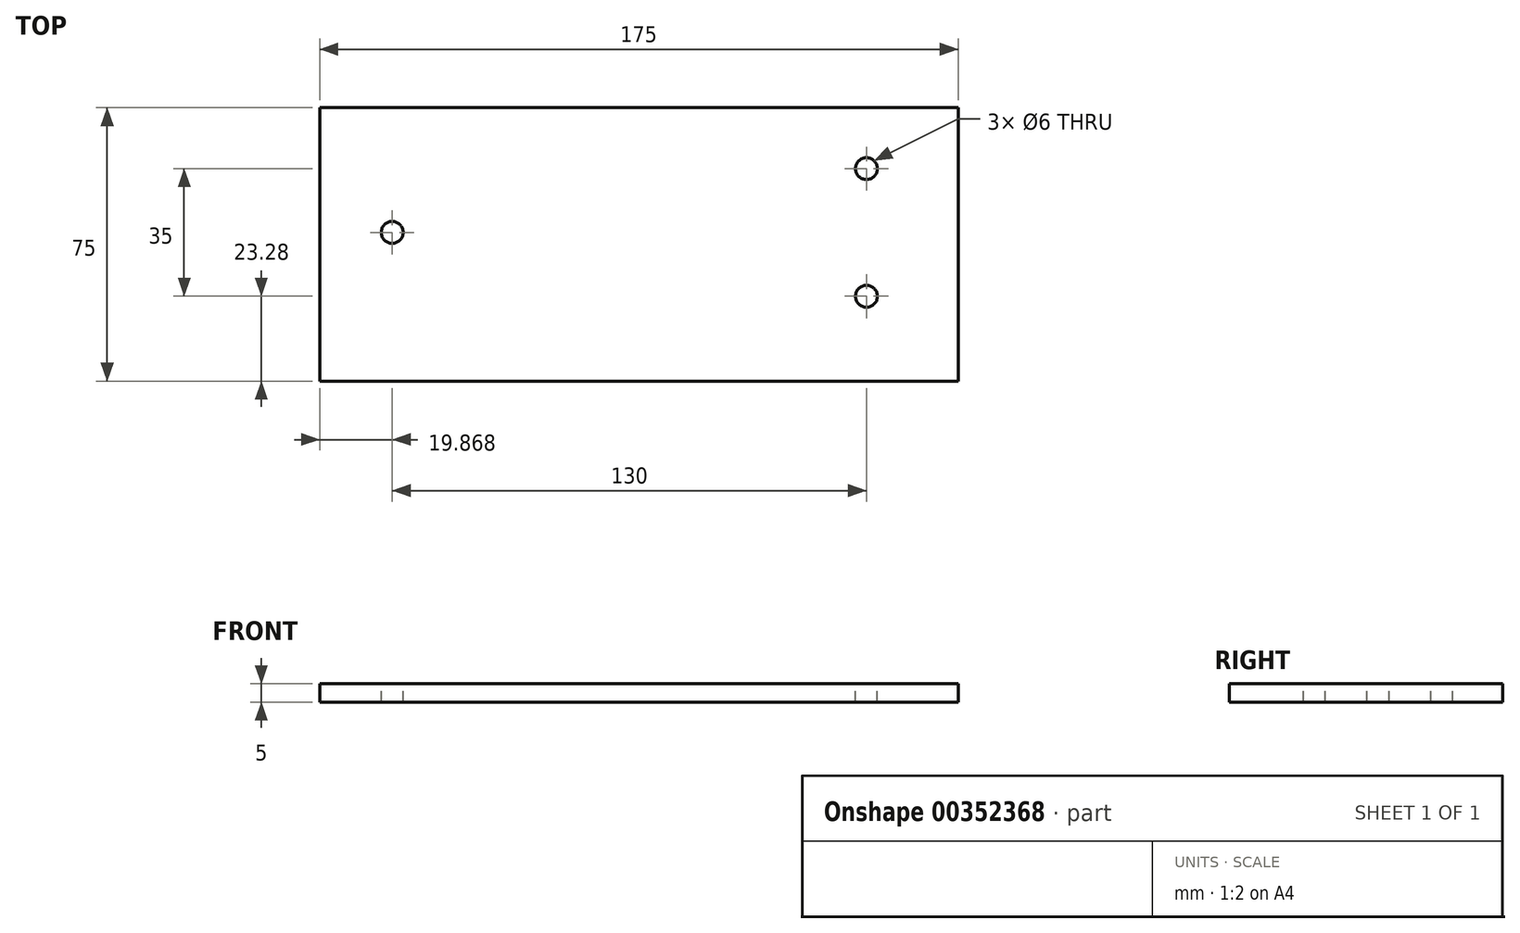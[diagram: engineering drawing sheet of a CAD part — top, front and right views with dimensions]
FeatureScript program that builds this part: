
annotation { "Feature Type Name" : "Feature", "Feature Type Description" : "" }
export const myFeature = defineFeature(function(context is Context, id is Id, definition is map)
    precondition{}
    {
        {
            var Q0;
            Q0=qCreatedBy(makeId("Top.planeOp"),FACE);
            var sketch = newSketch(context, id + "F0", { "sketchPlane" : qUnion([Q0])});
            skLineSegment(sketch, "E0.bottom", {"start": v(-83, 34.22) * mm, "end": v(92, 34.22) * mm});
            skLineSegment(sketch, "E0.top", {"start": v(-83, -40.78) * mm, "end": v(92, -40.78) * mm});
            skLineSegment(sketch, "E0.left", {"start": v(-83, 34.22) * mm, "end": v(-83, -40.78) * mm});
            skLineSegment(sketch, "E0.right", {"start": v(92, 34.22) * mm, "end": v(92, -40.78) * mm});
            skSolve(sketch);
        }
        {
            var Q0;
            Q0 = qSketchRegion(id + "F0", true);
            extrude(context, id + "F1", {"entities" : qUnion([Q0]), "depth" : 5 * mm});
        }
        {
            var Q0;
            Q0=makeQuery(id+"F1.opExtrude","CAP_FACE",FACE,{"disambiguationData":[OSD([sQuery(id+"F0.wireOp",EDGE,"E0.bottom"),sQuery(id+"F0.wireOp",EDGE,"E0.top"),sQuery(id+"F0.wireOp",EDGE,"E0.left"),sQuery(id+"F0.wireOp",EDGE,"E0.right")])],"isStart":false});
            var sketch = newSketch(context, id + "F2", { "sketchPlane" : qUnion([Q0])});
            skCircle(sketch, "E1", {"center": v(-63.13, 0) * mm, "radius": 3 * mm});
            skCircle(sketch, "E2", {"center": v(66.87, 17.5) * mm, "radius": 3 * mm});
            skCircle(sketch, "E3", {"center": v(66.87, -17.5) * mm, "radius": 3 * mm});
            skSolve(sketch);
        }
        {
            var Q0;
            Q0=makeQuery(id+"F2.imprint","IMPRINT",FACE,{"disambiguationData":[TD([[makeQuery(id+"F2.imprint","IMPRINT",EDGE,{"derivedFrom":sQuery(id+"F2.wireOp",EDGE,"E1")}),1.0]])]});
            var Q1;
            Q1 = qSketchRegion(id + "F2", true);
            extrude(context, id + "F3", {"entities" : qUnion([Q0, Q1]), "operationType" : NewBodyOperationType.REMOVE, "endBound" : BoundingType.THROUGH_ALL, "oppositeDirection" : true, "depth" : 25 * mm});
        }
    });
